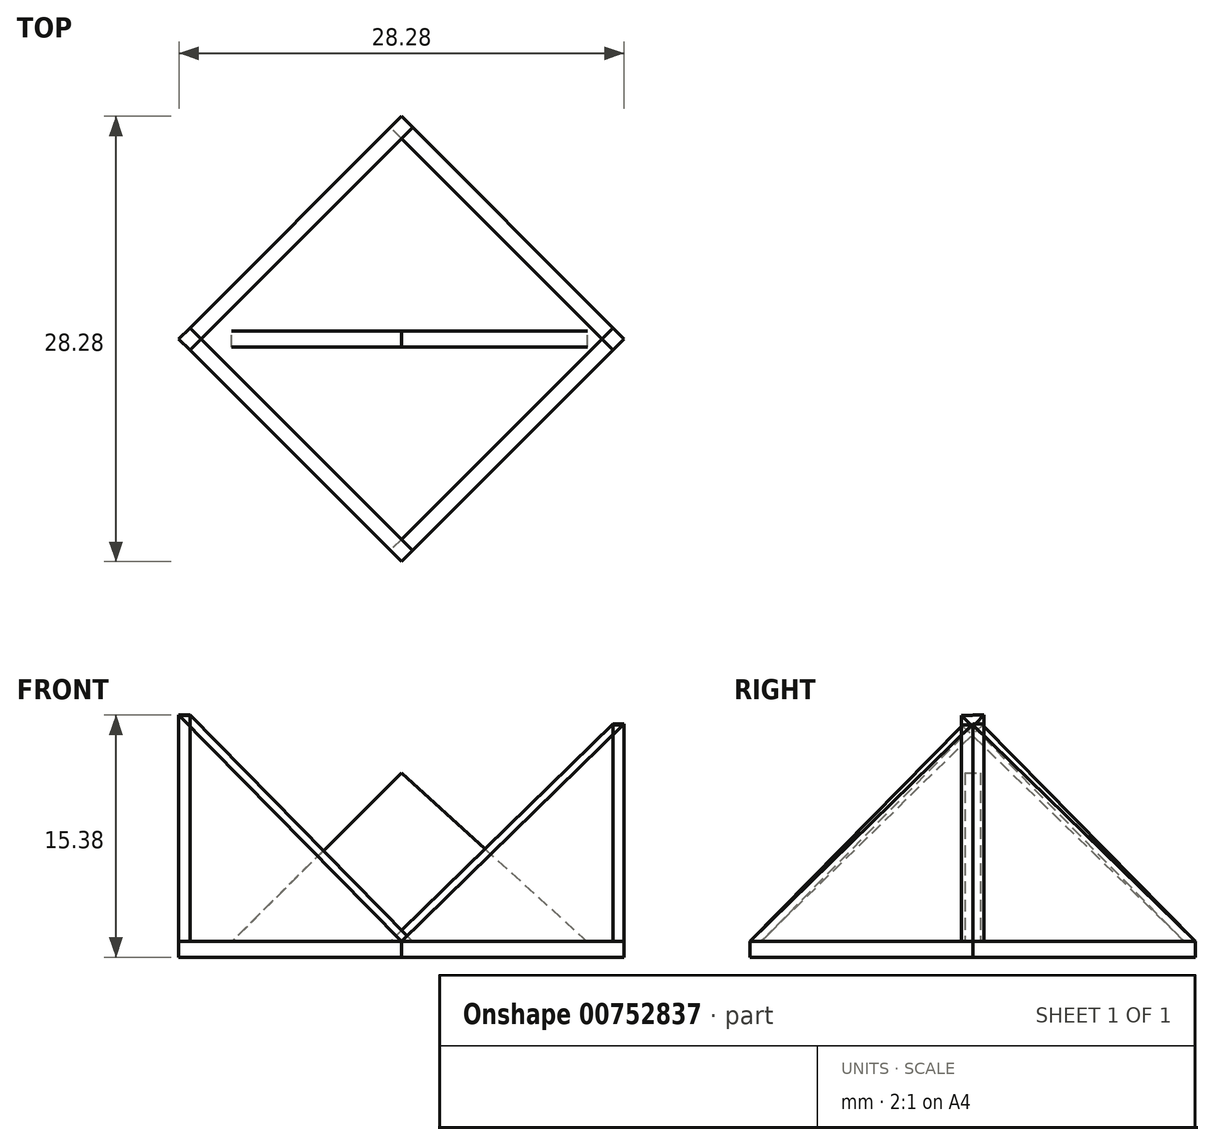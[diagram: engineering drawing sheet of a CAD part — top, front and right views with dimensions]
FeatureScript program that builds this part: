
annotation { "Feature Type Name" : "Feature", "Feature Type Description" : "" }
export const myFeature = defineFeature(function(context is Context, id is Id, definition is map)
    precondition{}
    {
        {
            var Q0;
            Q0=qCreatedBy(makeId("Top.planeOp"),FACE);
            var sketch = newSketch(context, id + "F0", { "sketchPlane" : qUnion([Q0])});
            skLineSegment(sketch, "E0", {"start": v(-14.14, 0) * mm, "end": v(0, 14.14) * mm});
            skLineSegment(sketch, "E1", {"start": v(0, 14.14) * mm, "end": v(14.14, 0) * mm});
            skLineSegment(sketch, "E2", {"start": v(14.14, 0) * mm, "end": v(0, -14.14) * mm});
            skLineSegment(sketch, "E3", {"start": v(0, -14.14) * mm, "end": v(-14.14, 0) * mm});
            skSolve(sketch);
        }
        {
            var Q0;
            Q0 = qSketchRegion(id + "F0", true);
            extrude(context, id + "F1", {"entities" : qUnion([Q0]), "depth" : 1 * mm, "offsetDistance" : 25 * mm});
        }
        {
            var Q0;
            Q0=qCreatedBy(makeId("Front.planeOp"),FACE);
            var sketch = newSketch(context, id + "F2", { "sketchPlane" : qUnion([Q0])});
            skLineSegment(sketch, "E4", {"start": v(-10.8, 0.97) * mm, "end": v(11.81, 0.97) * mm});
            skLineSegment(sketch, "E5", {"start": v(11.81, 0.97) * mm, "end": v(0, 11.7) * mm});
            skLineSegment(sketch, "E6", {"start": v(0, 11.7) * mm, "end": v(-10.8, 0.97) * mm});
            skSolve(sketch);
        }
        {
            var Q0;
            Q0 = qSketchRegion(id + "F2", true);
            extrude(context, id + "F3", {"entities" : qUnion([Q0]), "endBound" : BoundingType.SYMMETRIC, "depth" : 1 * mm, "offsetDistance" : 25 * mm});
        }
        {
            var Q0;
            Q0=makeQuery(id+"F1.opExtrude","SWEPT_FACE",FACE,{"disambiguationData":[OSD([sQuery(id+"F0.wireOp",EDGE,"E0")])]});
            var sketch = newSketch(context, id + "F4", { "sketchPlane" : qUnion([Q0])});
            skLineSegment(sketch, "E7", {"start": v(-10, 1) * mm, "end": v(10, 1) * mm});
            skLineSegment(sketch, "E8", {"start": v(10, 1) * mm, "end": v(10, 15.37) * mm});
            skLineSegment(sketch, "E9", {"start": v(10, 15.37) * mm, "end": v(-10, 1) * mm});
            skSolve(sketch);
        }
        {
            var Q0;
            Q0 = qSketchRegion(id + "F4", true);
            extrude(context, id + "F5", {"entities" : qUnion([Q0]), "oppositeDirection" : true, "depth" : 1 * mm, "offsetDistance" : 25 * mm});
        }
        {
            var Q0;
            Q0=makeQuery(id+"F1.opExtrude","SWEPT_FACE",FACE,{"disambiguationData":[OSD([sQuery(id+"F0.wireOp",EDGE,"E3")])]});
            var sketch = newSketch(context, id + "F6", { "sketchPlane" : qUnion([Q0])});
            skLineSegment(sketch, "E10", {"start": v(-10, 1) * mm, "end": v(10, 1) * mm});
            skLineSegment(sketch, "E11", {"start": v(-10, 1) * mm, "end": v(-10, 15.38) * mm});
            skLineSegment(sketch, "E12", {"start": v(-10, 15.38) * mm, "end": v(10, 1) * mm});
            skSolve(sketch);
        }
        {
            var Q0;
            Q0 = qSketchRegion(id + "F6", true);
            extrude(context, id + "F7", {"entities" : qUnion([Q0]), "oppositeDirection" : true, "depth" : 1 * mm, "offsetDistance" : 25 * mm});
        }
        {
            var Q0;
            Q0=makeQuery(id+"F1.opExtrude","SWEPT_FACE",FACE,{"disambiguationData":[OSD([sQuery(id+"F0.wireOp",EDGE,"E2")])]});
            var sketch = newSketch(context, id + "F8", { "sketchPlane" : qUnion([Q0])});
            skLineSegment(sketch, "E13", {"start": v(-10, 1) * mm, "end": v(10, 1) * mm});
            skLineSegment(sketch, "E14", {"start": v(10, 1) * mm, "end": v(10, 14.83) * mm});
            skLineSegment(sketch, "E15", {"start": v(10, 14.83) * mm, "end": v(-10, 1) * mm});
            skSolve(sketch);
        }
        {
            var Q0;
            Q0 = qSketchRegion(id + "F8", true);
            extrude(context, id + "F9", {"entities" : qUnion([Q0]), "oppositeDirection" : true, "depth" : 1 * mm, "offsetDistance" : 25 * mm});
        }
        {
            var Q0;
            Q0=makeQuery(id+"F1.opExtrude","SWEPT_FACE",FACE,{"disambiguationData":[OSD([sQuery(id+"F0.wireOp",EDGE,"E1")])]});
            var sketch = newSketch(context, id + "F10", { "sketchPlane" : qUnion([Q0])});
            skLineSegment(sketch, "E16", {"start": v(10, 1) * mm, "end": v(-10, 1) * mm});
            skLineSegment(sketch, "E17", {"start": v(-10, 1) * mm, "end": v(-10, 14.76) * mm});
            skLineSegment(sketch, "E18", {"start": v(-10, 14.76) * mm, "end": v(10, 1) * mm});
            skSolve(sketch);
        }
        {
            var Q0;
            Q0 = qSketchRegion(id + "F10", true);
            extrude(context, id + "F11", {"entities" : qUnion([Q0]), "oppositeDirection" : true, "depth" : 1 * mm, "offsetDistance" : 25 * mm});
        }
    });
